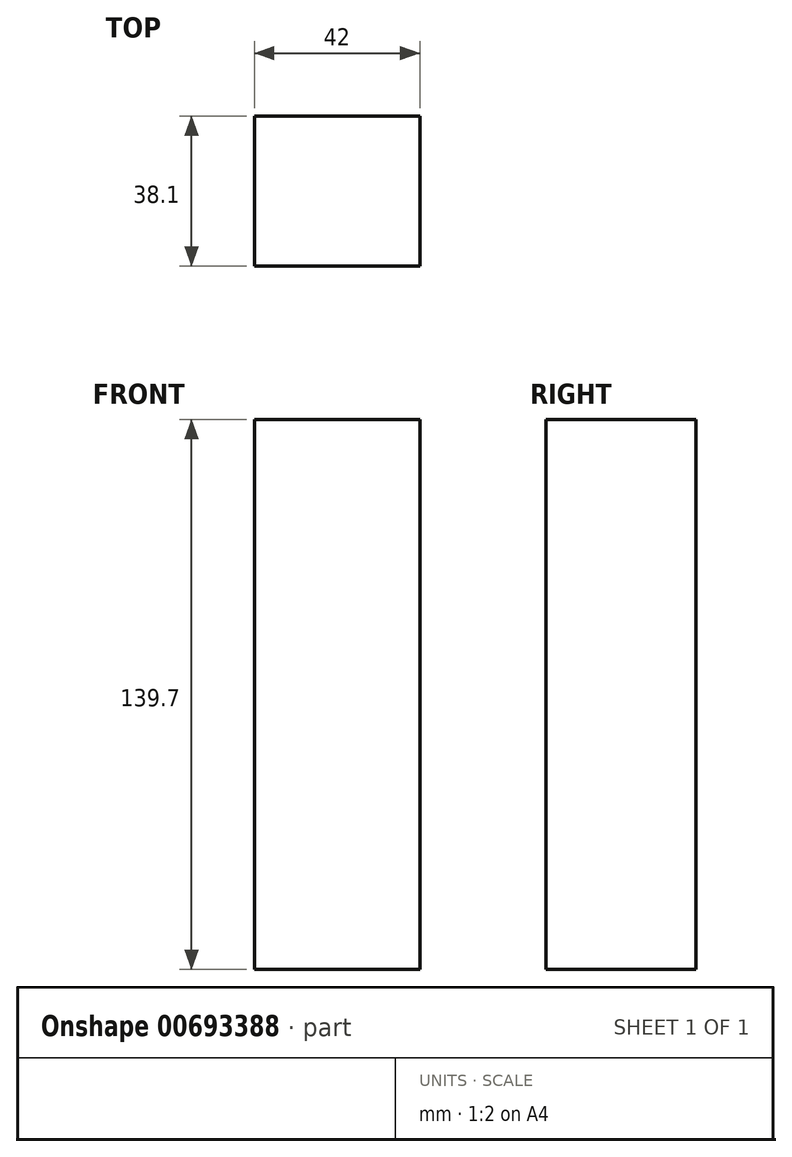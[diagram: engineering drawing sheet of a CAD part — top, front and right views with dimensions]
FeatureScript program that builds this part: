
annotation { "Feature Type Name" : "Feature", "Feature Type Description" : "" }
export const myFeature = defineFeature(function(context is Context, id is Id, definition is map)
    precondition{}
    {
        {
            assignVariable(context, id + "F0", {"name" : "L", "anyValue" : 42});
        }
        {
            var Q0;
            Q0=qCreatedBy(makeId("Right.planeOp"),FACE);
            var sketch = newSketch(context, id + "F1", { "sketchPlane" : qUnion([Q0])});
            skLineSegment(sketch, "E0.bottom", {"start": v(-49.9, 121.25) * mm, "end": v(-11.8, 121.25) * mm});
            skLineSegment(sketch, "E0.top", {"start": v(-49.9, -18.45) * mm, "end": v(-11.8, -18.45) * mm});
            skLineSegment(sketch, "E0.left", {"start": v(-49.9, 121.25) * mm, "end": v(-49.9, -18.45) * mm});
            skLineSegment(sketch, "E0.right", {"start": v(-11.8, 121.25) * mm, "end": v(-11.8, -18.45) * mm});
            skSolve(sketch);
        }
        {
            var Q0;
            Q0 = qSketchRegion(id + "F1", true);
            extrude(context, id + "F2", {"entities" : qUnion([Q0]), "depth" : (getVariable(context, 'L')) * mm, "offsetDistance" : 25.4 * mm});
        }
    });
